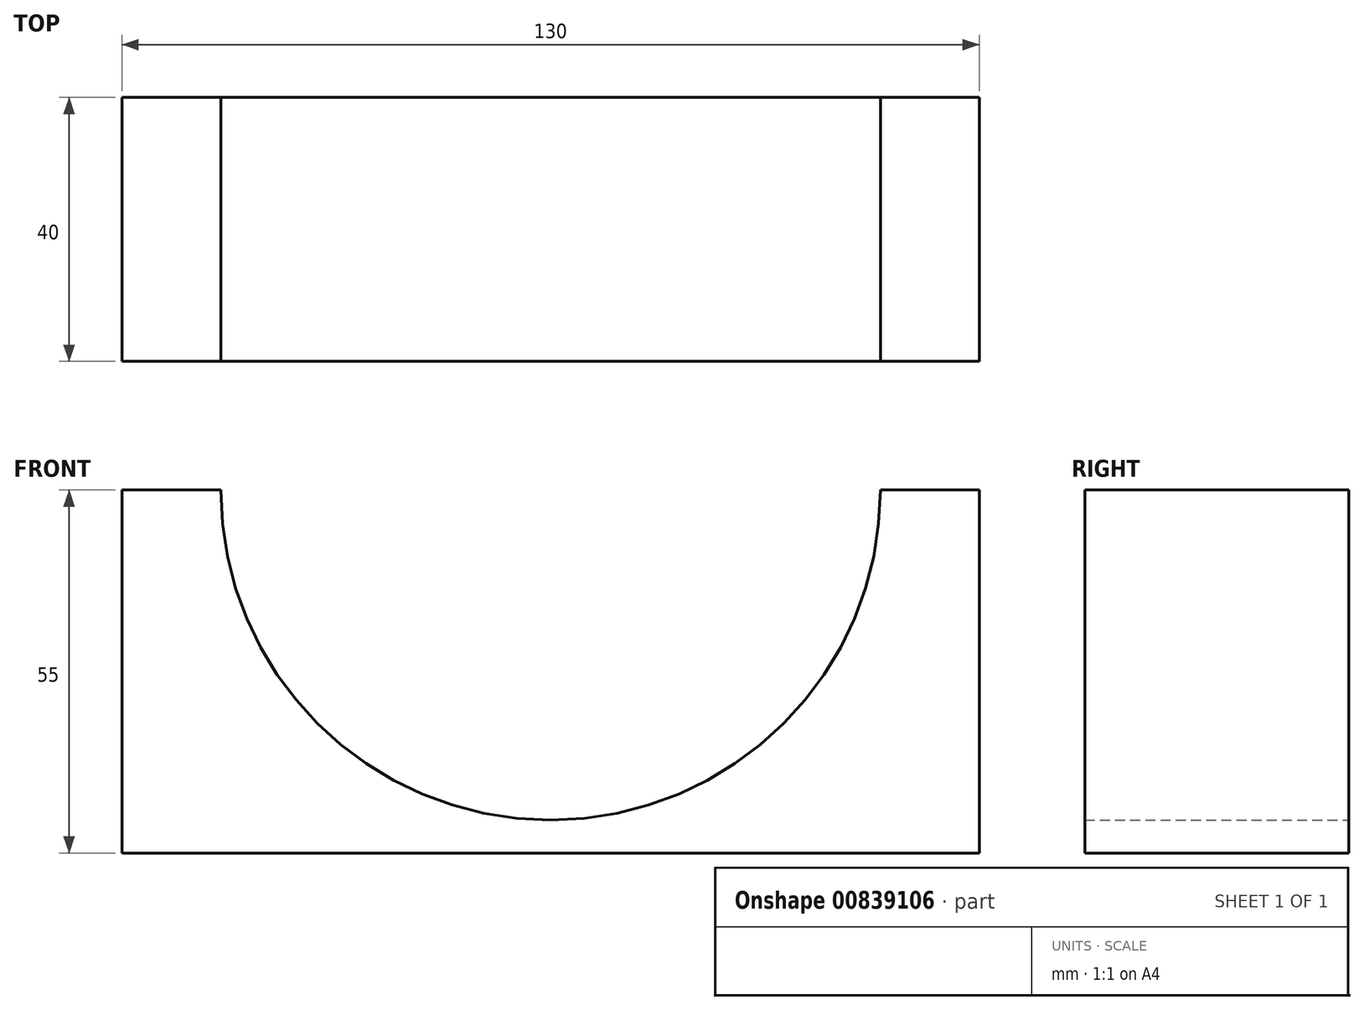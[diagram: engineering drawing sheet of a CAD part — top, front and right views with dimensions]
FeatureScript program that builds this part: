
annotation { "Feature Type Name" : "Feature", "Feature Type Description" : "" }
export const myFeature = defineFeature(function(context is Context, id is Id, definition is map)
    precondition{}
    {
        {
            var Q0;
            Q0=qCreatedBy(makeId("Front.planeOp"),FACE);
            var sketch = newSketch(context, id + "F0", { "sketchPlane" : qUnion([Q0])});
            skLineSegment(sketch, "E0", {"start": v(-64.4, 8.78) * mm, "end": v(-64.4, -46.22) * mm});
            skLineSegment(sketch, "E1", {"start": v(-64.4, -46.22) * mm, "end": v(65.6, -46.22) * mm});
            skLineSegment(sketch, "E2", {"start": v(65.6, -46.22) * mm, "end": v(65.6, 8.78) * mm});
            skPoint(sketch, "E3", {"position": v(0.6, -46.22) * mm});
            skLineSegment(sketch, "E4", {"start": v(-64.4, 8.78) * mm, "end": v(-49.4, 8.78) * mm});
            skLineSegment(sketch, "E5", {"start": v(65.6, 8.78) * mm, "end": v(50.6, 8.78) * mm});
            skArc(sketch, "E6", {"start": v(-49.4, 8.78) * mm, "mid": v(0.6, -41.22) * mm, "end": v(50.6, 8.78) * mm});
            skSolve(sketch);
        }
        {
            var Q0;
            Q0=makeQuery(id+"F0.imprint","IMPRINT",FACE,{"disambiguationData":[TD([[makeQuery(id+"F0.imprint","IMPRINT",EDGE,{"derivedFrom":sQuery(id+"F0.wireOp",EDGE,"E0")}),1.0]])]});
            extrude(context, id + "F1", {"entities" : qUnion([Q0]), "endBound" : BoundingType.SYMMETRIC, "depth" : 40 * mm, "offsetDistance" : 25 * mm});
        }
    });
